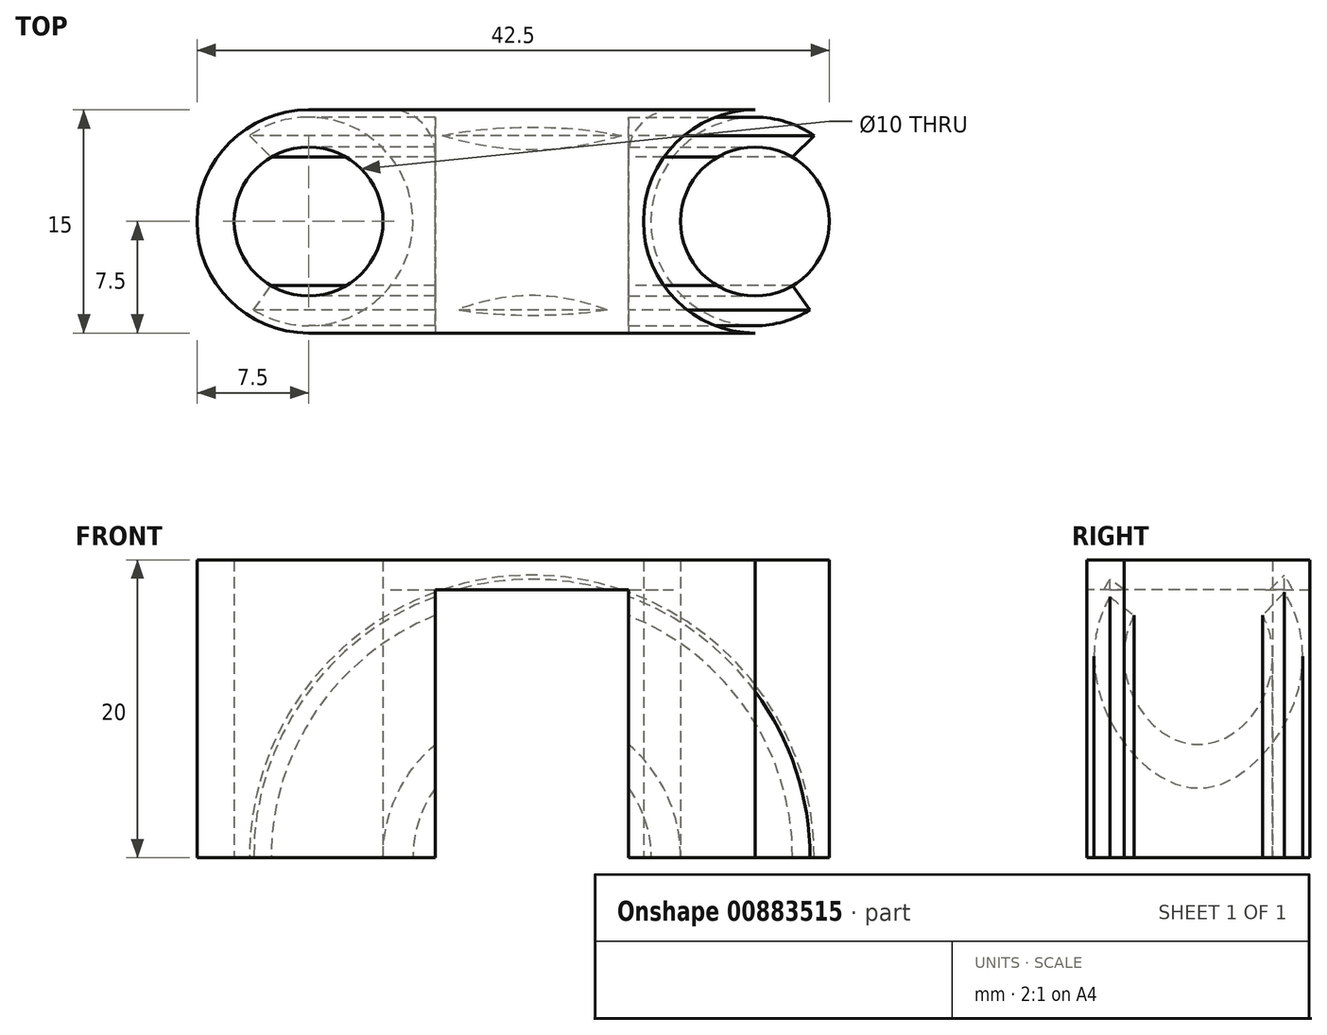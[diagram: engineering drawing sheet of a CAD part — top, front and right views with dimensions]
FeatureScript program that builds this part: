
annotation { "Feature Type Name" : "Feature", "Feature Type Description" : "" }
export const myFeature = defineFeature(function(context is Context, id is Id, definition is map)
    precondition{}
    {
        {
            var Q0;
            Q0=qCreatedBy(makeId("Top.planeOp"),FACE);
            var sketch = newSketch(context, id + "F0", { "sketchPlane" : qUnion([Q0])});
            skCircle(sketch, "E0", {"center": v(-15, 0) * mm, "radius": 7.5 * mm});
            skLineSegment(sketch, "E1", {"start": v(-15, 7.5) * mm, "end": v(0, 7.5) * mm});
            skLineSegment(sketch, "E2", {"start": v(-15, -7.5) * mm, "end": v(5, -7.5) * mm});
            skLineSegment(sketch, "E3.MirrorCS", {"start": v(15, 7.5) * mm, "end": v(0, 7.5) * mm});
            skCircle(sketch, "E4.MirrorC", {"center": v(15, 0) * mm, "radius": 7.5 * mm});
            skLineSegment(sketch, "E5.MirrorCS", {"start": v(15, -7.5) * mm, "end": v(0, -7.5) * mm});
            skCircle(sketch, "E6.0", {"center": v(-15, 0) * mm, "radius": 5 * mm});
            skCircle(sketch, "E7.MirrorC", {"center": v(15, 0) * mm, "radius": 5 * mm});
            skSolve(sketch);
        }
        {
            var Q0;
            {var subQ2=sQuery(id+"F0.wireOp",EDGE,"E1");Q0=makeQuery(id+"F0.imprint","IMPRINT",FACE,{"disambiguationData":[TD([[makeQuery(id+"F0.imprint","IMPRINT",EDGE,{"derivedFrom":subQ2}),-1.0]])]});}
            var Q1;
            Q1=makeQuery(id+"F0.imprint","IMPRINT",FACE,{"disambiguationData":[TD([[makeQuery(id+"F0.imprint","IMPRINT",EDGE,{"derivedFrom":sQuery(id+"F0.wireOp",EDGE,"E6.0")}),-1.0]])]});
            var Q2;
            Q2=makeQuery(id+"F0.imprint","IMPRINT",FACE,{"disambiguationData":[TD([[makeQuery(id+"F0.imprint","IMPRINT",EDGE,{"derivedFrom":sQuery(id+"F0.wireOp",EDGE,"E7.MirrorC")}),1.0]])]});
            extrude(context, id + "F1", {"entities" : qUnion([Q0, Q1, Q2]), "depth" : 20 * mm, "offsetDistance" : 25 * mm});
        }
        {
            var Q0;
            Q0=qCreatedBy(makeId("Top.planeOp"),FACE);
            var sketch = newSketch(context, id + "F2", { "sketchPlane" : qUnion([Q0])});
            skArc(sketch, "E8", {"start": v(-18.7, -5.95) * mm, "mid": v(-8, 0.17) * mm, "end": v(-18.98, 5.77) * mm});
            skLineSegment(sketch, "E9", {"start": v(0, -7.86) * mm, "end": v(0, 17.82) * mm});
            skArc(sketch, "E10.0", {"start": v(-17.52, -4.32) * mm, "mid": v(-10, 0) * mm, "end": v(-17.52, 4.32) * mm});
            skLineSegment(sketch, "E11", {"start": v(-18.7, -5.95) * mm, "end": v(-17.52, -4.32) * mm});
            skLineSegment(sketch, "E12.MirrorCS", {"start": v(-18.98, 5.77) * mm, "end": v(-17.52, 4.32) * mm});
            skSolve(sketch);
        }
        {
            var Q0;
            Q0=makeQuery(id+"F2.imprint","IMPRINT",FACE,{"disambiguationData":[TD([[makeQuery(id+"F2.imprint","IMPRINT",EDGE,{"derivedFrom":sQuery(id+"F2.wireOp",EDGE,"E8")}),1.0]])]});
            var Q1;
            Q1=sQuery(id+"F2.wireOp",EDGE,"E9");
            revolve(context, id + "F3", {"surfaceOperationType" : NewSurfaceOperationType.NEW, "entities" : qUnion([Q0]), "axis" : qUnion([Q1]), "revolveType" : RevolveType.ONE_DIRECTION, "angle" : 180 * degree});
        }
        {
            var Q0;
            Q0=makeQuery(id+"F1.opExtrude","SWEPT_FACE",FACE,{"disambiguationData":[OSD([sQuery(id+"F0.wireOp",EDGE,"E2"),sQuery(id+"F0.wireOp",EDGE,"E5.MirrorCS")])]});
            var sketch = newSketch(context, id + "F4", { "sketchPlane" : qUnion([Q0])});
            skLineSegment(sketch, "E13.bottom", {"start": v(-6.5, 0) * mm, "end": v(6.5, 0) * mm});
            skLineSegment(sketch, "E13.top", {"start": v(-6.5, 18) * mm, "end": v(6.5, 18) * mm});
            skLineSegment(sketch, "E13.left", {"start": v(-6.5, 0) * mm, "end": v(-6.5, 18) * mm});
            skLineSegment(sketch, "E13.right", {"start": v(6.5, 0) * mm, "end": v(6.5, 18) * mm});
            skPoint(sketch, "E14", {"position": v(0, 18) * mm});
            skSolve(sketch);
        }
        {
            var Q0;
            Q0=makeQuery(id+"F4.imprint","IMPRINT",FACE,{"disambiguationData":[TD([[makeQuery(id+"F4.imprint","IMPRINT",EDGE,{"derivedFrom":sQuery(id+"F4.wireOp",EDGE,"E13.bottom")}),1.0]])]});
            extrude(context, id + "F5", {"entities" : qUnion([Q0]), "operationType" : NewBodyOperationType.REMOVE, "oppositeDirection" : true, "depth" : 25 * mm, "offsetDistance" : 25 * mm});
        }
        {
            var Q0;
            Q0=makeQuery(id+"F5.boolean.opBoolean","COPY",EDGE,{"derivedFrom":makeQuery(id+"F5.opExtrude","CAP_EDGE",EDGE,{"disambiguationData":[OSD([sQuery(id+"F4.wireOp",EDGE,"E13.left")])],"isStart":true})});
            var Q1;
            Q1=makeQuery(id+"F5.boolean.opBoolean","INTERSECT",EDGE,{"derivedFrom":[makeQuery(id+"F1.opExtrude","SWEPT_FACE",FACE,{"disambiguationData":[OSD([sQuery(id+"F0.wireOp",EDGE,"E1"),sQuery(id+"F0.wireOp",EDGE,"E3.MirrorCS")])]}),makeQuery(id+"F5.opExtrude","SWEPT_FACE",FACE,{"disambiguationData":[OSD([sQuery(id+"F4.wireOp",EDGE,"E13.left")])]})]});
            var Q2;
            Q2=makeQuery(id+"F5.boolean.opBoolean","INTERSECT",EDGE,{"derivedFrom":[makeQuery(id+"F1.opExtrude","SWEPT_FACE",FACE,{"disambiguationData":[OSD([sQuery(id+"F0.wireOp",EDGE,"E1"),sQuery(id+"F0.wireOp",EDGE,"E3.MirrorCS")])]}),makeQuery(id+"F5.opExtrude","SWEPT_FACE",FACE,{"disambiguationData":[OSD([sQuery(id+"F4.wireOp",EDGE,"E13.right")])]})]});
            var Q3;
            Q3=makeQuery(id+"F5.boolean.opBoolean","COPY",EDGE,{"derivedFrom":makeQuery(id+"F5.opExtrude","CAP_EDGE",EDGE,{"disambiguationData":[OSD([sQuery(id+"F4.wireOp",EDGE,"E13.right")])],"isStart":true})});
            fillet(context, id + "F6", {"entities" : qUnion([Q0, Q1, Q2, Q3]), "radius" : 3 * mm, "tangentPropagation" : true, "allowEdgeOverflow" : false});
        }
    });
